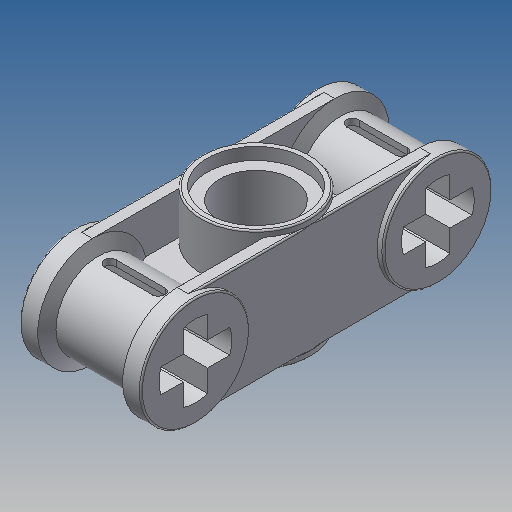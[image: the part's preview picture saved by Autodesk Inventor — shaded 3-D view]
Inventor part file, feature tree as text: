
AUTODESK INVENTOR PART (.ipt)
format: ipt  version: 2022.2 (Build 262287000, 287)  size: 397,824 bytes
history: native  units: in
note: dims shown in document units (in); Inventor stores cm internally (conversion verified against a paired STEP export)
features: extrude x6, sketch x4, mirror x2, plane x1, revolve x1, fillet x1
ambient origin geometry x8: Origin, YZ Plane, XZ Plane, XY Plane, X Axis, Y Axis, Z Axis, Center Point
bodies: Solid1 (feature_tree)
feature tree (15):
  sketch  "Sketch2"  dims[d0=0.2835in d1=0.189in]
  extrude  "Extrusion1"  Depth=0.189in
  plane  "Work Plane1"
  extrude  "Extrusion2"  Depth=0.315in TaperAngle=0.0deg
  extrude  "Extrusion4"  Depth=0.2835in
  extrude  "Extrusion3"  Depth=0.0039in TaperAngle=0.0deg
  mirror  "Mirror1"
  revolve  "Revolution1"  [1 undecoded]
  extrude  "Extrusion5"  Depth=0.0039in TaperAngle=0.0deg
  extrude  "Extrusion6"  Depth=0.0039in
  mirror  "Mirror2"
  fillet  "Fillet1"  Radius=0.0472in
  sketch  "Sketch3"  dims[d2=0.315in d3=0.315in d4=0.0in]
  sketch  "Sketch4"  dims[d5=0.0in d6=0.2835in]
  sketch  "Sketch5"  dims[d7=0.0315in d8=0.4724in d9=0.0in d10=0.252in d11=0.0315in d12=0.0in d13=0.2835in d14=0.0472in d15=0.315in d16=0.2205in d17=0.063in d18=0.0315in d19=0.1575in d20=90.0deg d21=0.063in d22=0.0in d23=0.063in d24=0.0in d25=0.189in d26=0.063in d27=0.063in d28=0.0in d29=0.0039in]
note: 1 required parameter value undecoded (feature->parameter linkage not recoverable at this tier; creation-order binding heuristic only, values carry confidence <= 0.55)
